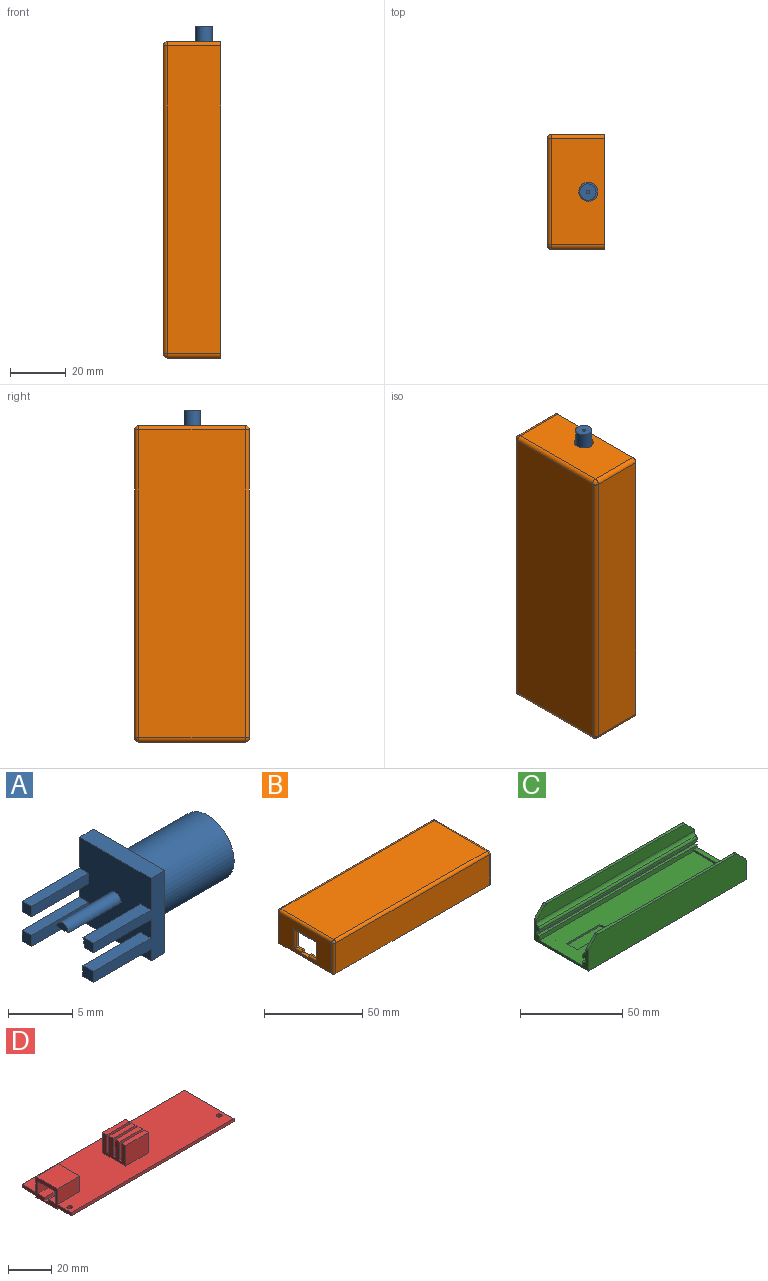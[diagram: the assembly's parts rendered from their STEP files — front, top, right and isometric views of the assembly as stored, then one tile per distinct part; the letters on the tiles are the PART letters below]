
ASSEMBLY  parts=4 mates=3
PART A: 30 faces, bbox 16.5x7.9x7.9 mm
  f0: plane 7.87x7.87mm, normal (0,-1,0), area 24.5mm2, adj f1,f3,f4,f8,f10,f11,f14,f23
  f1: plane 7.87x1.52mm, normal (0,0,-1), area 12mm2, adj f0,f2,f3,f4
  f2: plane 7.87x7.87mm, normal (0,1,0), area 24.9mm2, adj f1,f3,f4,f8,f15,f17,f18,f19
  f3: plane 7.87x7.87mm, normal (1,0,0), area 35.2mm2, adj f0,f1,f2,f6,f8
  f4: plane 7.87x7.87mm, normal (-1,0,0), area 57.1mm2, adj f0,f1,f2,f8,f10,f11,f12,f13
  f5: cylinder r=0.64mm len=8.64mm, axis (-1,0,0), area 34.5mm2, adj f7,f9
  f6: cylinder r=2.92mm len=8.64mm, axis (-1,0,0), area 158.5mm2, adj f3,f7
  f7: plane 5.84x5.84mm, normal (1,0,0), area 25.5mm2, adj f5,f6
  f8: plane 7.87x1.52mm, normal (0,0,1), area 12mm2, adj f0,f2,f3,f4
  f9: plane 1.27x1.27mm, normal (1,0,0), area 1.3mm2, adj f5
  f10: plane 6.35x1.15mm, normal (0,0,1), area 7.3mm2, adj f0,f4,f13,f14
  f11: plane 6.35x1.02mm, normal (0,0,-1), area 6.5mm2, adj f0,f4,f12,f14
  f12: cylinder r=2.92mm len=6.35mm, axis (-1,0,0), area 5.7mm2, adj f4,f11,f13,f14
  f13: plane 6.35x0.04mm, normal (0,1,0), area 0.2mm2, adj f4,f10,f12,f14
  f14: plane 1.15x0.92mm, normal (-1,0,0), area 1mm2, adj f0,f10,f11,f12,f13
  f15: plane 6.35x1mm, normal (0,0,1), area 6.4mm2, adj f2,f4,f16,f18
  f16: plane 6.35x0.99mm, normal (0,-1,0), area 6.3mm2, adj f4,f15,f17,f18
  f17: plane 6.35x1mm, normal (0,0,-1), area 6.4mm2, adj f2,f4,f16,f18
  f18: plane 1x0.99mm, normal (-1,0,0), area 1mm2, adj f2,f15,f16,f17
  f19: plane 6.35x1mm, normal (0,0,1), area 6.4mm2, adj f2,f4,f20,f22
  f20: plane 6.35x1.05mm, normal (0,-1,0), area 6.6mm2, adj f4,f19,f21,f22
  f21: plane 6.35x1mm, normal (0,0,-1), area 6.4mm2, adj f2,f4,f20,f22
  f22: plane 1.05x1mm, normal (-1,0,0), area 1.1mm2, adj f2,f19,f20,f21
  f23: plane 6.35x1.15mm, normal (0,0,1), area 7.3mm2, adj f0,f4,f25,f26
  f24: plane 6.35x1.15mm, normal (0,0,-1), area 7.3mm2, adj f0,f4,f25,f26
  f25: plane 6.35x1.05mm, normal (0,1,0), area 6.6mm2, adj f4,f23,f24,f26
  f26: plane 1.15x1.05mm, normal (-1,0,0), area 1.2mm2, adj f0,f23,f24,f25
  f27: plane 1.27x0.64mm, normal (-1,0,0), area 0.6mm2, adj f28,f29
  f28: cylinder r=0.64mm len=5.84mm, axis (-1,0,0), area 11.7mm2, adj f4,f27,f29
  f29: plane 5.84x1.27mm, normal (0,0,-1), area 7.4mm2, adj f4,f27,f28
PART B: 42 faces, bbox 113.5x41.1x20.6 mm
  f0: plane 38.1x19.05mm, normal (1,0,0), area 537.6mm2, adj f1,f3,f9,f10,f11,f12,f13,f14
  f1: plane 109.47x19.05mm, normal (0,-1,0), area 2085.5mm2, adj f0,f2,f9,f24
  f2: plane 38.1x19.05mm, normal (-1,0,0), area 688.9mm2, adj f1,f3,f9,f18,f24
  f3: plane 109.47x19.05mm, normal (0,1,0), area 2085.5mm2, adj f0,f2,f9,f24
  f4: plane 38.1x19.05mm, normal (-1,0,0), area 521.9mm2, adj f9,f12,f13,f14,f25,f29,f30,f37
  f5: plane 110.49x19.05mm, normal (0,-1,0), area 2104.8mm2, adj f9,f25,f27,f28
  f6: plane 38.1x19.05mm, normal (1,0,0), area 688.9mm2, adj f9,f18,f27,f33,f36
  f7: plane 110.49x19.05mm, normal (0,1,0), area 2104.8mm2, adj f9,f30,f34,f36
  f8: plane 110.49x38.1mm, normal (0,0,1), area 4209.7mm2, adj f28,f29,f33,f34
  f9: plane 113.54x41.15mm, normal (0,0,-1), area 498.9mm2, adj f0,f1,f2,f3,f4,f5,f6,f7
  f10: plane 10.16x1.02mm, normal (0,1,0), area 10.3mm2, adj f0,f11,f17,f40
  f11: plane 4.78x1.02mm, normal (0,0,1), area 4.9mm2, adj f0,f10,f12,f38
  f12: plane 2.03x1.52mm, normal (0,1,0), area 2.9mm2, adj f0,f4,f11,f13,f38
  f13: plane 5.08x2.03mm, normal (0,0,1), area 10.3mm2, adj f0,f4,f12,f14
  f14: plane 2.03x1.52mm, normal (0,-1,0), area 2.9mm2, adj f0,f4,f13,f15,f37
  f15: plane 4.61x1.02mm, normal (0,0,1), area 4.7mm2, adj f0,f14,f16,f37
  f16: plane 10.16x1.02mm, normal (0,-1,0), area 10.3mm2, adj f0,f15,f17,f39
  f17: plane 14.48x1.02mm, normal (0,0,-1), area 14.7mm2, adj f0,f10,f16,f41
  f18: cylinder r=3.43mm len=6.86mm, axis (1,0,0), area 43.8mm2, adj f2,f6
  f19: plane 8.83x0.64mm, normal (0,0,1), area 4.5mm2, adj f0,f20,f21,f23
  f20: plane 6.35x2.54mm, normal (1,0,0), area 16.1mm2, adj f19,f21,f22,f23
  f21: cylinder r=1.52mm len=3.78mm, axis (0,0,-1), area 4.5mm2, adj f0,f19,f20,f22
  f22: cylinder r=1.52mm len=8.83mm, axis (0,-1,0), area 10.8mm2, adj f0,f20,f21,f23
  f23: cylinder r=1.52mm len=3.78mm, axis (0,0,-1), area 4.5mm2, adj f0,f19,f20,f22
  f24: plane 109.47x38.1mm, normal (0,0,-1), area 4171mm2, adj f0,f1,f2,f3
  f25: cylinder r=1.52mm len=19.05mm, axis (0,0,-1), area 45.6mm2, adj f4,f5,f9,f26
  f26: sphere r=1.52mm, area 3.6mm2, adj f25,f28,f29
  f27: cylinder r=1.52mm len=19.05mm, axis (0,0,-1), area 45.6mm2, adj f5,f6,f9,f31
  f28: cylinder r=1.52mm len=110.49mm, axis (-1,0,0), area 264.5mm2, adj f5,f8,f26,f31
  f29: cylinder r=1.52mm len=38.1mm, axis (0,-1,0), area 91.2mm2, adj f4,f8,f26,f32
  f30: cylinder r=1.52mm len=19.05mm, axis (0,0,1), area 45.6mm2, adj f4,f7,f9,f32
  f31: sphere r=1.52mm, area 3.6mm2, adj f27,f28,f33
  f32: sphere r=1.52mm, area 3.6mm2, adj f29,f30,f34
  f33: cylinder r=1.52mm len=38.1mm, axis (0,-1,0), area 91.2mm2, adj f6,f8,f31,f35
  f34: cylinder r=1.52mm len=110.49mm, axis (1,0,0), area 264.5mm2, adj f7,f8,f32,f35
  f35: sphere r=1.52mm, area 3.6mm2, adj f33,f34,f36
  f36: cylinder r=1.52mm len=19.05mm, axis (0,0,1), area 45.6mm2, adj f6,f7,f9,f35
  f37: cylinder r=1.02mm len=5.63mm, axis (0,-1,0), area 8mm2, adj f4,f14,f15,f39
  f38: cylinder r=1.02mm len=5.8mm, axis (0,-1,0), area 8.2mm2, adj f4,f11,f12,f40
  f39: cylinder r=1.02mm len=12.19mm, axis (0,0,-1), area 17.4mm2, adj f4,f16,f37,f41
  f40: cylinder r=1.02mm len=12.19mm, axis (0,0,1), area 17.4mm2, adj f4,f10,f38,f41
  f41: cylinder r=1.02mm len=16.51mm, axis (0,1,0), area 24.3mm2, adj f4,f17,f39,f40
PART C: 45 faces, bbox 109.2x37.3x18.8 mm
  f0: plane 109.22x1.51mm, normal (0,-1,0), area 164.8mm2, adj f3,f4,f20,f44
  f1: plane 109.22x1.51mm, normal (0,1,0), area 164.8mm2, adj f3,f4,f25,f43
  f2: plane 95.26x1.52mm, normal (0,0,1), area 145.2mm2, adj f19,f26,f41,f42
  f3: plane 37.34x11.81mm, normal (1,0,0), area 135.6mm2, adj f0,f1,f9,f10,f12,f14,f15,f16
  f4: plane 37.34x11.81mm, normal (-1,0,0), area 113.5mm2, adj f0,f1,f9,f10,f15,f16,f18,f19
  f5: plane 22.86x1.02mm, normal (0,1,0), area 23.2mm2, adj f6,f8,f9,f28
  f6: plane 7.11x1.02mm, normal (1,0,0), area 7.2mm2, adj f5,f7,f9,f28
  f7: plane 22.86x1.02mm, normal (0,-1,0), area 23.2mm2, adj f6,f8,f9,f28
  f8: plane 7.11x1.02mm, normal (-1,0,0), area 7.2mm2, adj f5,f7,f9,f28
  f9: plane 109.22x30.23mm, normal (0,0,1), area 3083.2mm2, adj f3,f4,f5,f6,f7,f8,f11,f12
  f10: plane 109.22x37.34mm, normal (0,0,-1), area 4078.1mm2, adj f3,f4,f11,f16,f19
  f11: cylinder r=0.01mm len=1.52mm, axis (0,0,-1), area 0.1mm2, adj f9,f10
  f12: plane 2.54x1.02mm, normal (0,-1,0), area 2.6mm2, adj f3,f9,f13,f14
  f13: plane 21.84x1.02mm, normal (-1,0,0), area 22.2mm2, adj f9,f12,f14,f15
  f14: plane 21.84x2.54mm, normal (0,0,1), area 55.5mm2, adj f3,f12,f13,f15
  f15: plane 109.22x2.54mm, normal (0,-1,0), area 274.8mm2, adj f3,f4,f9,f13,f14,f22
  f16: plane 109.22x18.8mm, normal (0,1,0), area 2012.4mm2, adj f3,f4,f10,f17,f30,f32,f36,f37
  f17: plane 95.26x1.52mm, normal (0,0,1), area 145.2mm2, adj f16,f27,f37,f38
  f18: plane 109.22x2.54mm, normal (0,1,0), area 277.4mm2, adj f3,f4,f9,f23
  f19: plane 109.22x18.8mm, normal (0,-1,0), area 2012.4mm2, adj f2,f3,f4,f10,f29,f31,f35,f39
  f20: plane 109.22x1.52mm, normal (0,0,-1), area 166.5mm2, adj f0,f3,f4,f21
  f21: plane 109.22x2.29mm, normal (0,-1,0), area 249.7mm2, adj f3,f4,f20,f22
  f22: plane 109.22x1.52mm, normal (0,0,1), area 166.5mm2, adj f3,f4,f15,f21
  f23: plane 109.22x1.52mm, normal (0,0,1), area 166.5mm2, adj f3,f4,f18,f24
  f24: plane 109.22x2.29mm, normal (0,1,0), area 249.7mm2, adj f3,f4,f23,f25
  f25: plane 109.22x1.52mm, normal (0,0,-1), area 166.5mm2, adj f1,f3,f4,f24
  f26: plane 109.22x7.42mm, normal (0,1,0), area 769.6mm2, adj f2,f3,f4,f29,f31,f33,f35,f39
  f27: plane 109.22x7.42mm, normal (0,-1,0), area 769.6mm2, adj f3,f4,f17,f30,f32,f34,f36,f37
  f28: plane 22.86x7.11mm, normal (0,0,1), area 162.6mm2, adj f5,f6,f7,f8
  f29: plane 5.46x5.46mm, normal (-0.71,0,0.71), area 11.8mm2, adj f19,f26,f39,f41
  f30: plane 5.46x5.46mm, normal (-0.71,0,0.71), area 11.8mm2, adj f16,f27,f37,f40
  f31: plane 5.46x5.46mm, normal (0.71,0,0.71), area 11.8mm2, adj f19,f26,f35,f42
  f32: plane 5.46x5.46mm, normal (0.71,0,0.71), area 11.8mm2, adj f16,f27,f36,f38
  f33: cylinder r=2.54mm len=109.22mm, axis (1,0,0), area 290.5mm2, adj f3,f4,f26,f43
  f34: cylinder r=2.54mm len=109.22mm, axis (-1,0,0), area 290.5mm2, adj f3,f4,f27,f44
  f35: cylinder r=1.52mm len=1.52mm, axis (0,1,0), area 1.8mm2, adj f3,f19,f26,f31
  f36: cylinder r=1.52mm len=1.52mm, axis (0,1,0), area 1.8mm2, adj f3,f16,f27,f32
  f37: cylinder r=1.52mm len=1.52mm, axis (0,-1,0), area 1.8mm2, adj f16,f17,f27,f30
  f38: cylinder r=1.52mm len=1.52mm, axis (0,1,0), area 1.8mm2, adj f16,f17,f27,f32
  f39: cylinder r=1.52mm len=1.52mm, axis (0,-1,0), area 1.8mm2, adj f4,f19,f26,f29
  f40: cylinder r=1.52mm len=1.52mm, axis (0,-1,0), area 1.8mm2, adj f4,f16,f27,f30
  f41: cylinder r=1.52mm len=1.52mm, axis (0,-1,0), area 1.8mm2, adj f2,f19,f26,f29
  f42: cylinder r=1.52mm len=1.52mm, axis (0,1,0), area 1.8mm2, adj f2,f19,f26,f31
  f43: cylinder r=1.52mm len=109.22mm, axis (1,0,0), area 174.3mm2, adj f1,f3,f4,f33
  f44: cylinder r=1.52mm len=109.22mm, axis (-1,0,0), area 174.3mm2, adj f0,f3,f4,f34
PART D: 42 faces, bbox 106.7x32.3x14.4 mm
  f0: plane 32.26x11.58mm, normal (-1,0,0), area 112.4mm2, adj f5,f9,f10,f11,f12,f14,f15,f16
  f1: plane 14.99x2.79mm, normal (0,0,1), area 41.9mm2, adj f4,f21,f22,f31
  f2: plane 14.99x2.79mm, normal (0,0,1), area 41.9mm2, adj f4,f22,f28,f30
  f3: plane 14.99x2.79mm, normal (0,0,1), area 41.9mm2, adj f4,f22,f25,f27
  f4: plane 14.99x11.56mm, normal (1,0,0), area 134.5mm2, adj f1,f2,f3,f10,f20,f21,f23,f24
  f5: plane 106.68x1.78mm, normal (0,-1,0), area 189.7mm2, adj f0,f6,f10,f11
  f6: plane 32.26x1.78mm, normal (1,0,0), area 57.4mm2, adj f5,f9,f10,f11
  f7: cylinder r=1.27mm len=2.54mm, axis (0,0,-1), area 14.2mm2, adj f10,f11
  f8: cylinder r=1.27mm len=2.54mm, axis (0,0,-1), area 14.2mm2, adj f10,f11
  f9: plane 106.68x1.78mm, normal (0,1,0), area 189.7mm2, adj f0,f6,f10,f11
  f10: plane 106.68x32.26mm, normal (0,0,1), area 3000.8mm2, adj f0,f4,f5,f6,f7,f8,f9,f12
  f11: plane 106.68x32.26mm, normal (0,0,-1), area 3225.3mm2, adj f0,f5,f6,f7,f8,f9,f15,f16
  f12: plane 14.73x8.79mm, normal (0,1,0), area 129.5mm2, adj f0,f10,f13,f18
  f13: plane 13.97x8.79mm, normal (1,0,0), area 122.8mm2, adj f10,f12,f14,f18
  f14: plane 14.73x8.79mm, normal (0,-1,0), area 129.5mm2, adj f0,f10,f13,f18
  f15: plane 14.73x1.02mm, normal (0,1,0), area 15mm2, adj f0,f11,f17,f19
  f16: plane 14.73x1.02mm, normal (0,-1,0), area 15mm2, adj f0,f11,f17,f19
  f17: plane 13.97x1.02mm, normal (1,0,0), area 14.2mm2, adj f11,f15,f16,f19
  f18: plane 14.73x13.97mm, normal (0,0,1), area 205.8mm2, adj f0,f12,f13,f14
  f19: plane 14.73x13.97mm, normal (0,0,-1), area 205.8mm2, adj f0,f15,f16,f17
  f20: plane 14.99x2.79mm, normal (0,0,1), area 41.9mm2, adj f4,f22,f23,f24
  f21: plane 14.99x11.56mm, normal (0,1,0), area 173.2mm2, adj f1,f4,f10,f22
  f22: plane 14.99x11.56mm, normal (-1,0,0), area 134.5mm2, adj f1,f2,f3,f10,f20,f21,f23,f24
  f23: plane 14.99x11.56mm, normal (0,-1,0), area 173.2mm2, adj f4,f10,f20,f22
  f24: plane 14.99x10.16mm, normal (0,1,0), area 152.3mm2, adj f4,f20,f22,f26
  f25: plane 14.99x10.16mm, normal (0,-1,0), area 152.3mm2, adj f3,f4,f22,f26
  f26: plane 14.99x1.27mm, normal (0,0,1), area 19mm2, adj f4,f22,f24,f25
  f27: plane 14.99x10.16mm, normal (0,1,0), area 152.3mm2, adj f3,f4,f22,f29
  f28: plane 14.99x10.16mm, normal (0,-1,0), area 152.3mm2, adj f2,f4,f22,f29
  f29: plane 14.99x1.27mm, normal (0,0,1), area 19mm2, adj f4,f22,f27,f28
  f30: plane 14.99x10.16mm, normal (0,1,0), area 152.3mm2, adj f2,f4,f22,f32
  f31: plane 14.99x10.16mm, normal (0,-1,0), area 152.3mm2, adj f1,f4,f22,f32
  f32: plane 14.99x1.27mm, normal (0,0,1), area 19mm2, adj f4,f22,f30,f31
  f33: plane 12.7x6.86mm, normal (0,-1,0), area 87.1mm2, adj f0,f34,f40,f41
  f34: plane 12.7x4.55mm, normal (0,0,1), area 57.7mm2, adj f0,f33,f35,f41
  f35: plane 12.7x1.62mm, normal (0,-1,0), area 20.6mm2, adj f0,f34,f36,f41
  f36: plane 12.7x2.21mm, normal (0,0,1), area 28.1mm2, adj f0,f35,f37,f41
  f37: plane 12.7x1.62mm, normal (0,1,0), area 20.6mm2, adj f0,f36,f38,f41
  f38: plane 12.7x4.67mm, normal (0,0,1), area 59.4mm2, adj f0,f37,f39,f41
  f39: plane 12.7x6.86mm, normal (0,1,0), area 87.1mm2, adj f0,f38,f40,f41
  f40: plane 12.7x11.43mm, normal (0,0,-1), area 145.2mm2, adj f0,f33,f39,f41
  f41: plane 11.43x8.48mm, normal (-1,0,0), area 82mm2, adj f33,f34,f35,f36,f37,f38,f39,f40
PLACE A rot(axis=(0,-1,0),90deg) t=(110.99,-39.42,47.9)mm
PLACE B rot(axis=(0,-1,0),90deg) t=(103.56,-39.29,49.05)mm
PLACE C rot(axis=(0.71,0,-0.71),180deg) t=(115.24,-39.42,49.17)mm
PLACE D rot(axis=(0,-1,0),90deg) t=(110.92,-39.42,47.9)mm
MATE fastened A.f4 <-> D.f6  axis (0,0,-1) through (109.15,-39.42,101.24)mm
MATE fastened C.f3 <-> D.f0  axis (0,0,-1) through (110.03,-56.05,-5.44)mm
MATE fastened C.f4 <-> B.f2  axis (0,0,1) through (115.24,-20.75,103.78)mm
